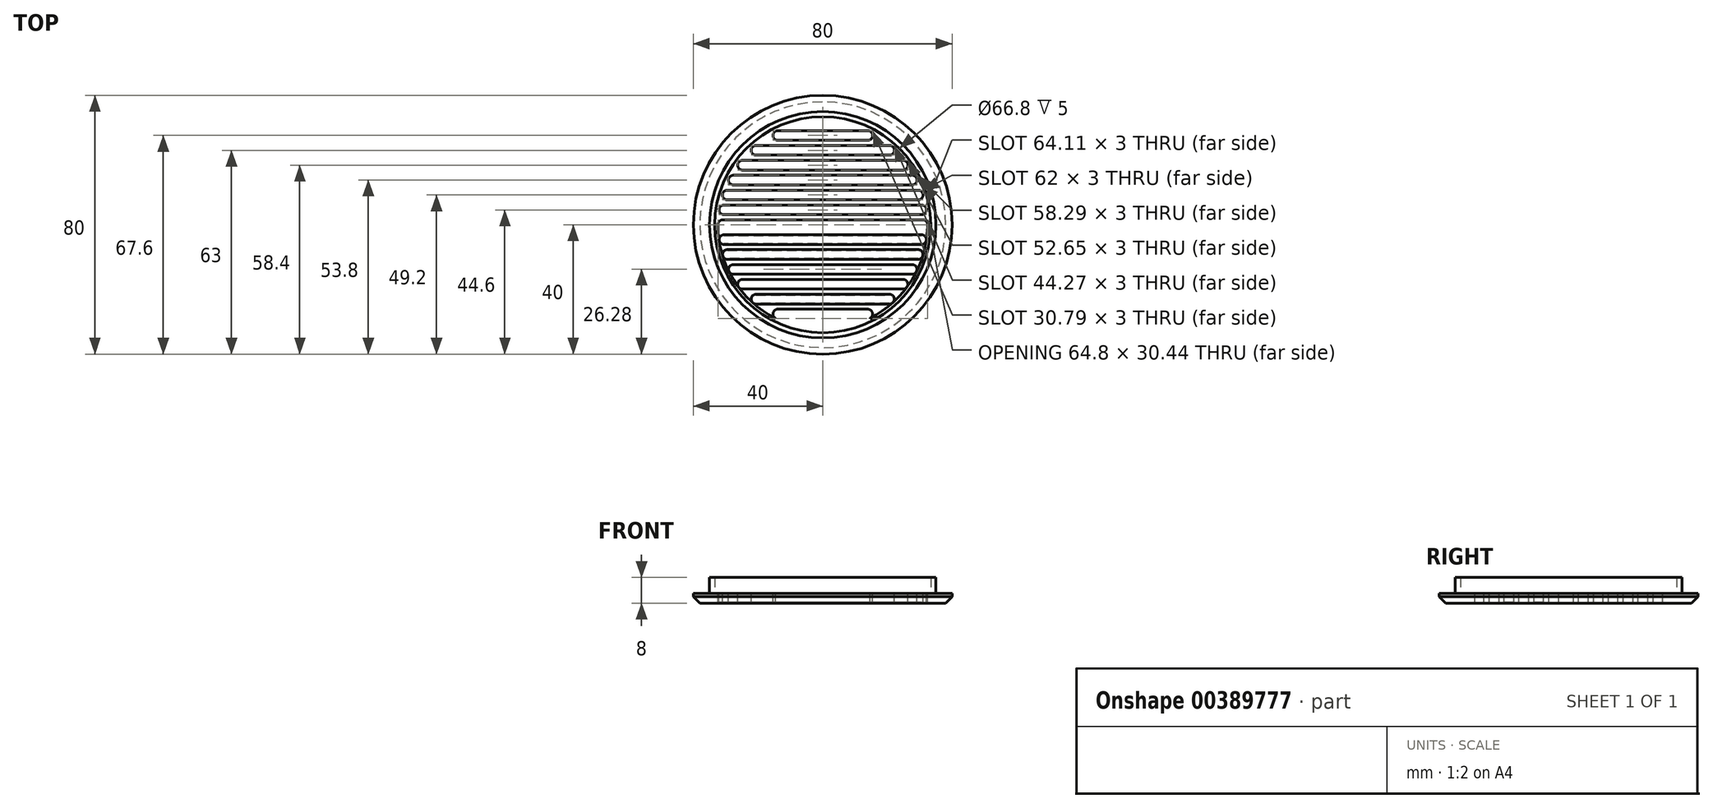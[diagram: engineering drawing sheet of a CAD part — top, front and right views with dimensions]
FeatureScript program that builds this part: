
annotation { "Feature Type Name" : "Feature", "Feature Type Description" : "" }
export const myFeature = defineFeature(function(context is Context, id is Id, definition is map)
    precondition{}
    {
        {
            var Q0;
            Q0=qCreatedBy(makeId("Top.planeOp"),FACE);
            var sketch = newSketch(context, id + "F0", { "sketchPlane" : qUnion([Q0])});
            skCircle(sketch, "E0", {"center": v(0, 0) * mm, "radius": 35 * mm});
            skCircle(sketch, "E1", {"center": v(0, 0) * mm, "radius": 40 * mm});
            skCircle(sketch, "E2", {"center": v(0, 0) * mm, "radius": 33.4 * mm});
            skSolve(sketch);
        }
        {
            var Q0;
            Q0=makeQuery(id+"F0.imprint","IMPRINT",FACE,{"disambiguationData":[TD([[makeQuery(id+"F0.imprint","IMPRINT",EDGE,{"derivedFrom":sQuery(id+"F0.wireOp",EDGE,"E0")}),1.0]])]});
            extrude(context, id + "F1", {"entities" : qUnion([Q0]), "depth" : 8 * mm});
        }
        {
            var Q0;
            Q0=makeQuery(id+"F0.imprint","IMPRINT",FACE,{"disambiguationData":[TD([[makeQuery(id+"F0.imprint","IMPRINT",EDGE,{"derivedFrom":sQuery(id+"F0.wireOp",EDGE,"E0")}),-1.0]])]});
            var Q1;
            Q1=makeQuery(id+"F0.imprint","IMPRINT",FACE,{"disambiguationData":[TD([[makeQuery(id+"F0.imprint","IMPRINT",EDGE,{"derivedFrom":sQuery(id+"F0.wireOp",EDGE,"E2")}),1.0]])]});
            extrude(context, id + "F2", {"entities" : qUnion([Q0, Q1]), "operationType" : NewBodyOperationType.ADD, "depth" : 3 * mm});
        }
        {
            var Q0;
            Q0=makeQuery(id+"F2.opExtrude","CAP_EDGE",EDGE,{"disambiguationData":[OSD([sQuery(id+"F0.wireOp",EDGE,"E1")])],"isStart":true});
            chamfer(context, id + "F3", {"entities" : qUnion([Q0]), "width" : 2 * mm, "tangentPropagation" : true});
        }
        {
            var Q0;
            Q0=makeQuery(id+"F2.opExtrude","CAP_FACE",FACE,{"disambiguationData":[OSD([sQuery(id+"F0.wireOp",EDGE,"E2")])],"isStart":false});
            var sketch = newSketch(context, id + "F4", { "sketchPlane" : qUnion([Q0])});
            skLineSegment(sketch, "E3.bottom", {"start": v(-30.9, 1.5) * mm, "end": v(30.9, 1.5) * mm});
            skLineSegment(sketch, "E3.top", {"start": v(-30.9, -1.5) * mm, "end": v(30.9, -1.5) * mm});
            skLineSegment(sketch, "E3.left", {"start": v(-32.4, 0) * mm, "end": v(-32.4, 0) * mm});
            skLineSegment(sketch, "E3.right", {"start": v(32.4, 0) * mm, "end": v(32.4, 0) * mm});
            skPoint(sketch, "E4.visualSharp", {"position": v(-32.4, 1.5) * mm});
            skArc(sketch, "E4.filletArc", {"start": v(-30.9, 1.5) * mm, "mid": v(-31.96, 1.06) * mm, "end": v(-32.4, 0) * mm});
            skPoint(sketch, "E5.visualSharp", {"position": v(-32.4, -1.5) * mm});
            skArc(sketch, "E5.filletArc", {"start": v(-32.4, 0) * mm, "mid": v(-31.96, -1.06) * mm, "end": v(-30.9, -1.5) * mm});
            skPoint(sketch, "E6.visualSharp", {"position": v(32.4, 1.5) * mm});
            skArc(sketch, "E6.filletArc", {"start": v(32.4, 0) * mm, "mid": v(31.96, 1.06) * mm, "end": v(30.9, 1.5) * mm});
            skPoint(sketch, "E7.visualSharp", {"position": v(32.4, -1.5) * mm});
            skArc(sketch, "E7.filletArc", {"start": v(30.9, -1.5) * mm, "mid": v(31.96, -1.06) * mm, "end": v(32.4, 0) * mm});
            skLineSegment(sketch, "E8.bottom", {"start": v(-30.56, 6.1) * mm, "end": v(30.56, 6.1) * mm});
            skLineSegment(sketch, "E8.top", {"start": v(-30.56, 3.1) * mm, "end": v(30.56, 3.1) * mm});
            skLineSegment(sketch, "E8.left", {"start": v(-32.06, 4.6) * mm, "end": v(-32.06, 4.6) * mm});
            skLineSegment(sketch, "E8.right", {"start": v(32.06, 4.6) * mm, "end": v(32.06, 4.6) * mm});
            skLineSegment(sketch, "E9.bottom", {"start": v(-29.5, 10.7) * mm, "end": v(29.5, 10.7) * mm});
            skLineSegment(sketch, "E9.top", {"start": v(-29.5, 7.7) * mm, "end": v(29.5, 7.7) * mm});
            skLineSegment(sketch, "E9.left", {"start": v(-31, 9.2) * mm, "end": v(-31, 9.2) * mm});
            skLineSegment(sketch, "E9.right", {"start": v(31, 9.2) * mm, "end": v(31, 9.2) * mm});
            skLineSegment(sketch, "E10.bottom", {"start": v(-27.65, 15.3) * mm, "end": v(27.65, 15.3) * mm});
            skLineSegment(sketch, "E10.top", {"start": v(-27.65, 12.3) * mm, "end": v(27.65, 12.3) * mm});
            skLineSegment(sketch, "E10.left", {"start": v(-29.15, 13.8) * mm, "end": v(-29.15, 13.8) * mm});
            skLineSegment(sketch, "E10.right", {"start": v(29.15, 13.8) * mm, "end": v(29.15, 13.8) * mm});
            skLineSegment(sketch, "E11.bottom", {"start": v(-24.82, 19.9) * mm, "end": v(24.82, 19.9) * mm});
            skLineSegment(sketch, "E11.top", {"start": v(-24.82, 16.9) * mm, "end": v(24.82, 16.9) * mm});
            skLineSegment(sketch, "E11.left", {"start": v(-26.32, 18.4) * mm, "end": v(-26.32, 18.4) * mm});
            skLineSegment(sketch, "E11.right", {"start": v(26.32, 18.4) * mm, "end": v(26.32, 18.4) * mm});
            skLineSegment(sketch, "E12.bottom", {"start": v(-20.64, 24.5) * mm, "end": v(20.64, 24.5) * mm});
            skLineSegment(sketch, "E12.top", {"start": v(-20.64, 21.5) * mm, "end": v(20.64, 21.5) * mm});
            skLineSegment(sketch, "E12.left", {"start": v(-22.14, 23) * mm, "end": v(-22.14, 23) * mm});
            skLineSegment(sketch, "E12.right", {"start": v(22.14, 23) * mm, "end": v(22.14, 23) * mm});
            skLineSegment(sketch, "E13.bottom", {"start": v(-13.9, 29.1) * mm, "end": v(13.9, 29.1) * mm});
            skLineSegment(sketch, "E13.top", {"start": v(-13.9, 26.1) * mm, "end": v(13.9, 26.1) * mm});
            skLineSegment(sketch, "E13.left", {"start": v(-15.4, 27.6) * mm, "end": v(-15.4, 27.6) * mm});
            skLineSegment(sketch, "E13.right", {"start": v(15.4, 27.6) * mm, "end": v(15.4, 27.6) * mm});
            skPoint(sketch, "E14.visualSharp", {"position": v(-32.06, 3.1) * mm});
            skArc(sketch, "E14.filletArc", {"start": v(-32.06, 4.6) * mm, "mid": v(-31.62, 3.54) * mm, "end": v(-30.56, 3.1) * mm});
            skPoint(sketch, "E15.visualSharp", {"position": v(-32.06, 6.1) * mm});
            skArc(sketch, "E15.filletArc", {"start": v(-30.56, 6.1) * mm, "mid": v(-31.62, 5.66) * mm, "end": v(-32.06, 4.6) * mm});
            skPoint(sketch, "E16.visualSharp", {"position": v(-31, 7.7) * mm});
            skArc(sketch, "E16.filletArc", {"start": v(-31, 9.2) * mm, "mid": v(-30.56, 8.14) * mm, "end": v(-29.5, 7.7) * mm});
            skPoint(sketch, "E17.visualSharp", {"position": v(-31, 10.7) * mm});
            skArc(sketch, "E17.filletArc", {"start": v(-29.5, 10.7) * mm, "mid": v(-30.56, 10.26) * mm, "end": v(-31, 9.2) * mm});
            skPoint(sketch, "E18.visualSharp", {"position": v(-29.15, 12.3) * mm});
            skArc(sketch, "E18.filletArc", {"start": v(-29.15, 13.8) * mm, "mid": v(-28.7, 12.74) * mm, "end": v(-27.65, 12.3) * mm});
            skPoint(sketch, "E19.visualSharp", {"position": v(-29.15, 15.3) * mm});
            skArc(sketch, "E19.filletArc", {"start": v(-27.65, 15.3) * mm, "mid": v(-28.7, 14.86) * mm, "end": v(-29.15, 13.8) * mm});
            skPoint(sketch, "E20.visualSharp", {"position": v(-26.32, 16.9) * mm});
            skArc(sketch, "E20.filletArc", {"start": v(-26.32, 18.4) * mm, "mid": v(-25.89, 17.34) * mm, "end": v(-24.82, 16.9) * mm});
            skPoint(sketch, "E21.visualSharp", {"position": v(-26.32, 19.9) * mm});
            skArc(sketch, "E21.filletArc", {"start": v(-24.82, 19.9) * mm, "mid": v(-25.89, 19.46) * mm, "end": v(-26.32, 18.4) * mm});
            skPoint(sketch, "E22.visualSharp", {"position": v(-22.14, 21.5) * mm});
            skArc(sketch, "E22.filletArc", {"start": v(-22.14, 23) * mm, "mid": v(-21.7, 21.94) * mm, "end": v(-20.64, 21.5) * mm});
            skPoint(sketch, "E23.visualSharp", {"position": v(-22.14, 24.5) * mm});
            skArc(sketch, "E23.filletArc", {"start": v(-20.64, 24.5) * mm, "mid": v(-21.7, 24.06) * mm, "end": v(-22.14, 23) * mm});
            skPoint(sketch, "E24.visualSharp", {"position": v(-15.4, 26.1) * mm});
            skArc(sketch, "E24.filletArc", {"start": v(-15.4, 27.6) * mm, "mid": v(-14.95, 26.54) * mm, "end": v(-13.9, 26.1) * mm});
            skPoint(sketch, "E25.visualSharp", {"position": v(-15.4, 29.1) * mm});
            skArc(sketch, "E25.filletArc", {"start": v(-13.9, 29.1) * mm, "mid": v(-14.95, 28.66) * mm, "end": v(-15.4, 27.6) * mm});
            skPoint(sketch, "E26.visualSharp", {"position": v(15.4, 29.1) * mm});
            skArc(sketch, "E26.filletArc", {"start": v(15.4, 27.6) * mm, "mid": v(14.95, 28.66) * mm, "end": v(13.9, 29.1) * mm});
            skPoint(sketch, "E27.visualSharp", {"position": v(15.4, 26.1) * mm});
            skArc(sketch, "E27.filletArc", {"start": v(13.9, 26.1) * mm, "mid": v(14.95, 26.54) * mm, "end": v(15.4, 27.6) * mm});
            skPoint(sketch, "E28.visualSharp", {"position": v(22.14, 24.5) * mm});
            skArc(sketch, "E28.filletArc", {"start": v(22.14, 23) * mm, "mid": v(21.7, 24.06) * mm, "end": v(20.64, 24.5) * mm});
            skPoint(sketch, "E29.visualSharp", {"position": v(22.14, 21.5) * mm});
            skArc(sketch, "E29.filletArc", {"start": v(20.64, 21.5) * mm, "mid": v(21.7, 21.94) * mm, "end": v(22.14, 23) * mm});
            skPoint(sketch, "E30.visualSharp", {"position": v(26.32, 19.9) * mm});
            skArc(sketch, "E30.filletArc", {"start": v(26.32, 18.4) * mm, "mid": v(25.89, 19.46) * mm, "end": v(24.82, 19.9) * mm});
            skPoint(sketch, "E31.visualSharp", {"position": v(26.32, 16.9) * mm});
            skArc(sketch, "E31.filletArc", {"start": v(24.82, 16.9) * mm, "mid": v(25.89, 17.34) * mm, "end": v(26.32, 18.4) * mm});
            skPoint(sketch, "E32.visualSharp", {"position": v(29.15, 15.3) * mm});
            skArc(sketch, "E32.filletArc", {"start": v(29.15, 13.8) * mm, "mid": v(28.7, 14.86) * mm, "end": v(27.65, 15.3) * mm});
            skPoint(sketch, "E33.visualSharp", {"position": v(29.15, 12.3) * mm});
            skArc(sketch, "E33.filletArc", {"start": v(27.65, 12.3) * mm, "mid": v(28.7, 12.74) * mm, "end": v(29.15, 13.8) * mm});
            skPoint(sketch, "E34.visualSharp", {"position": v(31, 10.7) * mm});
            skArc(sketch, "E34.filletArc", {"start": v(31, 9.2) * mm, "mid": v(30.56, 10.26) * mm, "end": v(29.5, 10.7) * mm});
            skPoint(sketch, "E35.visualSharp", {"position": v(31, 7.7) * mm});
            skArc(sketch, "E35.filletArc", {"start": v(29.5, 7.7) * mm, "mid": v(30.56, 8.14) * mm, "end": v(31, 9.2) * mm});
            skPoint(sketch, "E36.visualSharp", {"position": v(32.06, 6.1) * mm});
            skArc(sketch, "E36.filletArc", {"start": v(32.06, 4.6) * mm, "mid": v(31.62, 5.66) * mm, "end": v(30.56, 6.1) * mm});
            skPoint(sketch, "E37.visualSharp", {"position": v(32.06, 3.1) * mm});
            skArc(sketch, "E37.filletArc", {"start": v(30.56, 3.1) * mm, "mid": v(31.62, 3.54) * mm, "end": v(32.06, 4.6) * mm});
            skCircle(sketch, "E38.0", {"center": v(0, 0) * mm, "radius": 32.4 * mm});
            skArc(sketch, "E39.MirrorCS", {"start": v(-15.4, -27.6) * mm, "mid": v(-14.95, -26.54) * mm, "end": v(-13.9, -26.1) * mm});
            skArc(sketch, "E40.MirrorCS", {"start": v(-26.32, -18.4) * mm, "mid": v(-25.89, -17.34) * mm, "end": v(-24.82, -16.9) * mm});
            skArc(sketch, "E41.MirrorCS", {"start": v(29.5, -7.7) * mm, "mid": v(30.56, -8.14) * mm, "end": v(31, -9.2) * mm});
            skArc(sketch, "E42.MirrorCS", {"start": v(30.56, -3.1) * mm, "mid": v(31.62, -3.54) * mm, "end": v(32.06, -4.6) * mm});
            skArc(sketch, "E43.MirrorCS", {"start": v(-22.14, -23) * mm, "mid": v(-21.7, -21.94) * mm, "end": v(-20.64, -21.5) * mm});
            skArc(sketch, "E44.MirrorCS", {"start": v(27.65, -12.3) * mm, "mid": v(28.7, -12.74) * mm, "end": v(29.15, -13.8) * mm});
            skArc(sketch, "E45.MirrorCS", {"start": v(15.4, -27.6) * mm, "mid": v(14.95, -28.66) * mm, "end": v(13.9, -29.1) * mm});
            skArc(sketch, "E46.MirrorCS", {"start": v(20.64, -21.5) * mm, "mid": v(21.7, -21.94) * mm, "end": v(22.14, -23) * mm});
            skArc(sketch, "E47.MirrorCS", {"start": v(-29.15, -13.8) * mm, "mid": v(-28.7, -12.74) * mm, "end": v(-27.65, -12.3) * mm});
            skArc(sketch, "E48.MirrorCS", {"start": v(31, -9.2) * mm, "mid": v(30.56, -10.26) * mm, "end": v(29.5, -10.7) * mm});
            skArc(sketch, "E49.MirrorCS", {"start": v(13.9, -26.1) * mm, "mid": v(14.95, -26.54) * mm, "end": v(15.4, -27.6) * mm});
            skArc(sketch, "E50.MirrorCS", {"start": v(32.06, -4.6) * mm, "mid": v(31.62, -5.66) * mm, "end": v(30.56, -6.1) * mm});
            skArc(sketch, "E51.MirrorCS", {"start": v(-24.82, -19.9) * mm, "mid": v(-25.89, -19.46) * mm, "end": v(-26.32, -18.4) * mm});
            skArc(sketch, "E52.MirrorCS", {"start": v(22.14, -23) * mm, "mid": v(21.7, -24.06) * mm, "end": v(20.64, -24.5) * mm});
            skArc(sketch, "E53.MirrorCS", {"start": v(-31, -9.2) * mm, "mid": v(-30.56, -8.14) * mm, "end": v(-29.5, -7.7) * mm});
            skArc(sketch, "E54.MirrorCS", {"start": v(-13.9, -29.1) * mm, "mid": v(-14.95, -28.66) * mm, "end": v(-15.4, -27.6) * mm});
            skArc(sketch, "E55.MirrorCS", {"start": v(29.15, -13.8) * mm, "mid": v(28.7, -14.86) * mm, "end": v(27.65, -15.3) * mm});
            skArc(sketch, "E56.MirrorCS", {"start": v(-32.06, -4.6) * mm, "mid": v(-31.62, -3.54) * mm, "end": v(-30.56, -3.1) * mm});
            skArc(sketch, "E57.MirrorCS", {"start": v(26.32, -18.4) * mm, "mid": v(25.89, -19.46) * mm, "end": v(24.82, -19.9) * mm});
            skArc(sketch, "E58.MirrorCS", {"start": v(-20.64, -24.5) * mm, "mid": v(-21.7, -24.06) * mm, "end": v(-22.14, -23) * mm});
            skArc(sketch, "E59.MirrorCS", {"start": v(-27.65, -15.3) * mm, "mid": v(-28.7, -14.86) * mm, "end": v(-29.15, -13.8) * mm});
            skArc(sketch, "E60.MirrorCS", {"start": v(-29.5, -10.7) * mm, "mid": v(-30.56, -10.26) * mm, "end": v(-31, -9.2) * mm});
            skArc(sketch, "E61.MirrorCS", {"start": v(24.82, -16.9) * mm, "mid": v(25.89, -17.34) * mm, "end": v(26.32, -18.4) * mm});
            skArc(sketch, "E62.MirrorCS", {"start": v(-30.56, -6.1) * mm, "mid": v(-31.62, -5.66) * mm, "end": v(-32.06, -4.6) * mm});
            skPoint(sketch, "E63.MirrorP", {"position": v(-32.06, -3.1) * mm});
            skPoint(sketch, "E64.MirrorP", {"position": v(-22.14, -24.5) * mm});
            skPoint(sketch, "E65.MirrorP", {"position": v(-22.14, -21.5) * mm});
            skPoint(sketch, "E66.MirrorP", {"position": v(26.32, -16.9) * mm});
            skLineSegment(sketch, "E67.MirrorCS", {"start": v(-26.32, -18.4) * mm, "end": v(-26.32, -18.4) * mm});
            skPoint(sketch, "E68.MirrorP", {"position": v(26.32, -19.9) * mm});
            skPoint(sketch, "E69.MirrorP", {"position": v(-29.15, -15.3) * mm});
            skLineSegment(sketch, "E70.MirrorCS", {"start": v(-13.9, -26.1) * mm, "end": v(13.9, -26.1) * mm});
            skLineSegment(sketch, "E71.MirrorCS", {"start": v(26.32, -18.4) * mm, "end": v(26.32, -18.4) * mm});
            skPoint(sketch, "E72.MirrorP", {"position": v(-32.06, -6.1) * mm});
            skPoint(sketch, "E73.MirrorP", {"position": v(31, -7.7) * mm});
            skLineSegment(sketch, "E74.MirrorCS", {"start": v(-32.06, -4.6) * mm, "end": v(-32.06, -4.6) * mm});
            skPoint(sketch, "E75.MirrorP", {"position": v(15.4, -26.1) * mm});
            skLineSegment(sketch, "E76.MirrorCS", {"start": v(-31, -9.2) * mm, "end": v(-31, -9.2) * mm});
            skPoint(sketch, "E77.MirrorP", {"position": v(-26.32, -16.9) * mm});
            skLineSegment(sketch, "E78.MirrorCS", {"start": v(22.14, -23) * mm, "end": v(22.14, -23) * mm});
            skPoint(sketch, "E79.MirrorP", {"position": v(32.06, -6.1) * mm});
            skPoint(sketch, "E80.MirrorP", {"position": v(22.14, -24.5) * mm});
            skPoint(sketch, "E81.MirrorP", {"position": v(-31, -10.7) * mm});
            skLineSegment(sketch, "E82.MirrorCS", {"start": v(-24.82, -19.9) * mm, "end": v(24.82, -19.9) * mm});
            skLineSegment(sketch, "E83.MirrorCS", {"start": v(-15.4, -27.6) * mm, "end": v(-15.4, -27.6) * mm});
            skLineSegment(sketch, "E84.MirrorCS", {"start": v(-27.65, -12.3) * mm, "end": v(27.65, -12.3) * mm});
            skLineSegment(sketch, "E85.MirrorCS", {"start": v(-13.9, -29.1) * mm, "end": v(13.9, -29.1) * mm});
            skPoint(sketch, "E86.MirrorP", {"position": v(29.15, -12.3) * mm});
            skLineSegment(sketch, "E87.MirrorCS", {"start": v(31, -9.2) * mm, "end": v(31, -9.2) * mm});
            skPoint(sketch, "E88.MirrorP", {"position": v(-15.4, -29.1) * mm});
            skLineSegment(sketch, "E89.MirrorCS", {"start": v(-20.64, -21.5) * mm, "end": v(20.64, -21.5) * mm});
            skLineSegment(sketch, "E90.MirrorCS", {"start": v(-27.65, -15.3) * mm, "end": v(27.65, -15.3) * mm});
            skLineSegment(sketch, "E91.MirrorCS", {"start": v(15.4, -27.6) * mm, "end": v(15.4, -27.6) * mm});
            skLineSegment(sketch, "E92.MirrorCS", {"start": v(-20.64, -24.5) * mm, "end": v(20.64, -24.5) * mm});
            skPoint(sketch, "E93.MirrorP", {"position": v(22.14, -21.5) * mm});
            skPoint(sketch, "E94.MirrorP", {"position": v(31, -10.7) * mm});
            skLineSegment(sketch, "E95.MirrorCS", {"start": v(29.15, -13.8) * mm, "end": v(29.15, -13.8) * mm});
            skPoint(sketch, "E96.MirrorP", {"position": v(-31, -7.7) * mm});
            skLineSegment(sketch, "E97.MirrorCS", {"start": v(-29.5, -7.7) * mm, "end": v(29.5, -7.7) * mm});
            skLineSegment(sketch, "E98.MirrorCS", {"start": v(-29.5, -10.7) * mm, "end": v(29.5, -10.7) * mm});
            skPoint(sketch, "E99.MirrorP", {"position": v(29.15, -15.3) * mm});
            skPoint(sketch, "E100.MirrorP", {"position": v(15.4, -29.1) * mm});
            skLineSegment(sketch, "E101.MirrorCS", {"start": v(32.06, -4.6) * mm, "end": v(32.06, -4.6) * mm});
            skLineSegment(sketch, "E102.MirrorCS", {"start": v(-24.82, -16.9) * mm, "end": v(24.82, -16.9) * mm});
            skPoint(sketch, "E103.MirrorP", {"position": v(-15.4, -26.1) * mm});
            skPoint(sketch, "E104.MirrorP", {"position": v(-29.15, -12.3) * mm});
            skLineSegment(sketch, "E105.MirrorCS", {"start": v(-30.56, -6.1) * mm, "end": v(30.56, -6.1) * mm});
            skPoint(sketch, "E106.MirrorP", {"position": v(32.06, -3.1) * mm});
            skLineSegment(sketch, "E107.MirrorCS", {"start": v(-22.14, -23) * mm, "end": v(-22.14, -23) * mm});
            skPoint(sketch, "E108.MirrorP", {"position": v(-26.32, -19.9) * mm});
            skLineSegment(sketch, "E109.MirrorCS", {"start": v(-30.56, -3.1) * mm, "end": v(30.56, -3.1) * mm});
            skLineSegment(sketch, "E110.MirrorCS", {"start": v(-29.15, -13.8) * mm, "end": v(-29.15, -13.8) * mm});
            skSolve(sketch);
        }
        {
            var Q0;
            {var subQ1=sQuery(id+"F4.wireOp",EDGE,"E13.bottom");Q0=makeQuery(id+"F4.imprint","IMPRINT",FACE,{"disambiguationData":[TD([[makeQuery(id+"F4.imprint","IMPRINT",EDGE,{"derivedFrom":subQ1}),-1.0]])]});}
            var Q1;
            {var subQ1=sQuery(id+"F4.wireOp",EDGE,"E12.bottom");Q1=makeQuery(id+"F4.imprint","IMPRINT",FACE,{"disambiguationData":[TD([[makeQuery(id+"F4.imprint","IMPRINT",EDGE,{"derivedFrom":subQ1}),-1.0]])]});}
            var Q2;
            {var subQ1=sQuery(id+"F4.wireOp",EDGE,"E11.bottom");Q2=makeQuery(id+"F4.imprint","IMPRINT",FACE,{"disambiguationData":[TD([[makeQuery(id+"F4.imprint","IMPRINT",EDGE,{"derivedFrom":subQ1}),-1.0]])]});}
            var Q3;
            {var subQ2=sQuery(id+"F4.wireOp",EDGE,"E10.bottom");Q3=makeQuery(id+"F4.imprint","IMPRINT",FACE,{"disambiguationData":[TD([[makeQuery(id+"F4.imprint","IMPRINT",EDGE,{"derivedFrom":subQ2}),-1.0]])]});}
            var Q4;
            {var subQ1=sQuery(id+"F4.wireOp",EDGE,"E9.bottom");Q4=makeQuery(id+"F4.imprint","IMPRINT",FACE,{"disambiguationData":[TD([[makeQuery(id+"F4.imprint","IMPRINT",EDGE,{"derivedFrom":subQ1}),-1.0]])]});}
            var Q5;
            {var subQ1=sQuery(id+"F4.wireOp",EDGE,"E8.bottom");Q5=makeQuery(id+"F4.imprint","IMPRINT",FACE,{"disambiguationData":[TD([[makeQuery(id+"F4.imprint","IMPRINT",EDGE,{"derivedFrom":subQ1}),-1.0]])]});}
            var Q6;
            Q6=makeQuery(id+"F4.imprint","IMPRINT",FACE,{"disambiguationData":[TD([[makeQuery(id+"F4.imprint","IMPRINT",EDGE,{"derivedFrom":sQuery(id+"F4.wireOp",EDGE,"E3.bottom")}),-1.0]])]});
            var Q7;
            {var subQ2=sQuery(id+"F4.wireOp",EDGE,"E42.MirrorCS");Q7=makeQuery(id+"F4.imprint","IMPRINT",FACE,{"disambiguationData":[TD([[makeQuery(id+"F4.imprint","IMPRINT",EDGE,{"derivedFrom":subQ2}),-1.0]])]});}
            var Q8;
            {var subQ5=sQuery(id+"F4.wireOp",EDGE,"E41.MirrorCS");Q8=makeQuery(id+"F4.imprint","IMPRINT",FACE,{"disambiguationData":[TD([[makeQuery(id+"F4.imprint","IMPRINT",EDGE,{"derivedFrom":subQ5}),-1.0]])]});}
            var Q9;
            {var subQ4=sQuery(id+"F4.wireOp",EDGE,"E44.MirrorCS");Q9=makeQuery(id+"F4.imprint","IMPRINT",FACE,{"disambiguationData":[TD([[makeQuery(id+"F4.imprint","IMPRINT",EDGE,{"derivedFrom":subQ4}),-1.0]])]});}
            var Q10;
            {var subQ7=sQuery(id+"F4.wireOp",EDGE,"E40.MirrorCS");Q10=makeQuery(id+"F4.imprint","IMPRINT",FACE,{"disambiguationData":[TD([[makeQuery(id+"F4.imprint","IMPRINT",EDGE,{"derivedFrom":subQ7}),-1.0]])]});}
            var Q11;
            {var subQ5=sQuery(id+"F4.wireOp",EDGE,"E43.MirrorCS");Q11=makeQuery(id+"F4.imprint","IMPRINT",FACE,{"disambiguationData":[TD([[makeQuery(id+"F4.imprint","IMPRINT",EDGE,{"derivedFrom":subQ5}),-1.0]])]});}
            var Q12;
            {var subQ5=sQuery(id+"F4.wireOp",EDGE,"E39.MirrorCS");Q12=makeQuery(id+"F4.imprint","IMPRINT",FACE,{"disambiguationData":[TD([[makeQuery(id+"F4.imprint","IMPRINT",EDGE,{"derivedFrom":subQ5}),-1.0]])]});}
            extrude(context, id + "F5", {"entities" : qUnion([Q0, Q1, Q2, Q3, Q4, Q5, Q6, Q7, Q8, Q9, Q10, Q11, Q12]), "operationType" : NewBodyOperationType.REMOVE, "oppositeDirection" : true, "depth" : 25 * mm});
        }
        {
            var Q0;
            {var subQ0=sQuery(id+"F0.wireOp",EDGE,"E2");var subQ1=sQuery(id+"F0.wireOp",EDGE,"E0");Q0=makeQuery(id+"F2.boolean.opBoolean","MERGE",FACE,{"derivedFrom":[makeQuery(id+"F1.opExtrude","CAP_FACE",FACE,{"disambiguationData":[OSD([subQ1,subQ0])],"isStart":true}),makeQuery(id+"F2.opExtrude","CAP_FACE",FACE,{"disambiguationData":[OSD([subQ1,sQuery(id+"F0.wireOp",EDGE,"E1")])],"isStart":true}),makeQuery(id+"F2.opExtrude","CAP_FACE",FACE,{"disambiguationData":[OSD([subQ0])],"isStart":true})]});}
            chamfer(context, id + "F6", {"entities" : qUnion([Q0]), "width" : .2 * mm, "tangentPropagation" : true});
        }
    });
